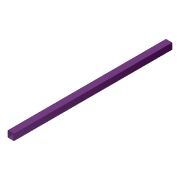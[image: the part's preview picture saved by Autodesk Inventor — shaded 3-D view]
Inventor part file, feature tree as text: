
AUTODESK INVENTOR PART (.ipt)
format: ipt  version: 2012 (Build 160160000, 160)  size: 76,288 bytes
history: native  units: in
note: dims shown in document units (in); Inventor stores cm internally (conversion verified against a paired STEP export)
features: extrude x1, shell x1, sketch x1
ambient origin geometry x8: Origin, YZ Plane, XZ Plane, XY Plane, X Axis, Y Axis, Z Axis, Center Point
bodies: Solid1 (feature_tree)
feature tree (3):
  extrude  "Extrusion1"  Depth=1.0in
  shell  "Shell1"  Thickness=26.0in
  sketch  "Sketch1"  dims[d0=1.0in d1=1.0in d2=26.0in d3=0.0in d4=0.0625in]
